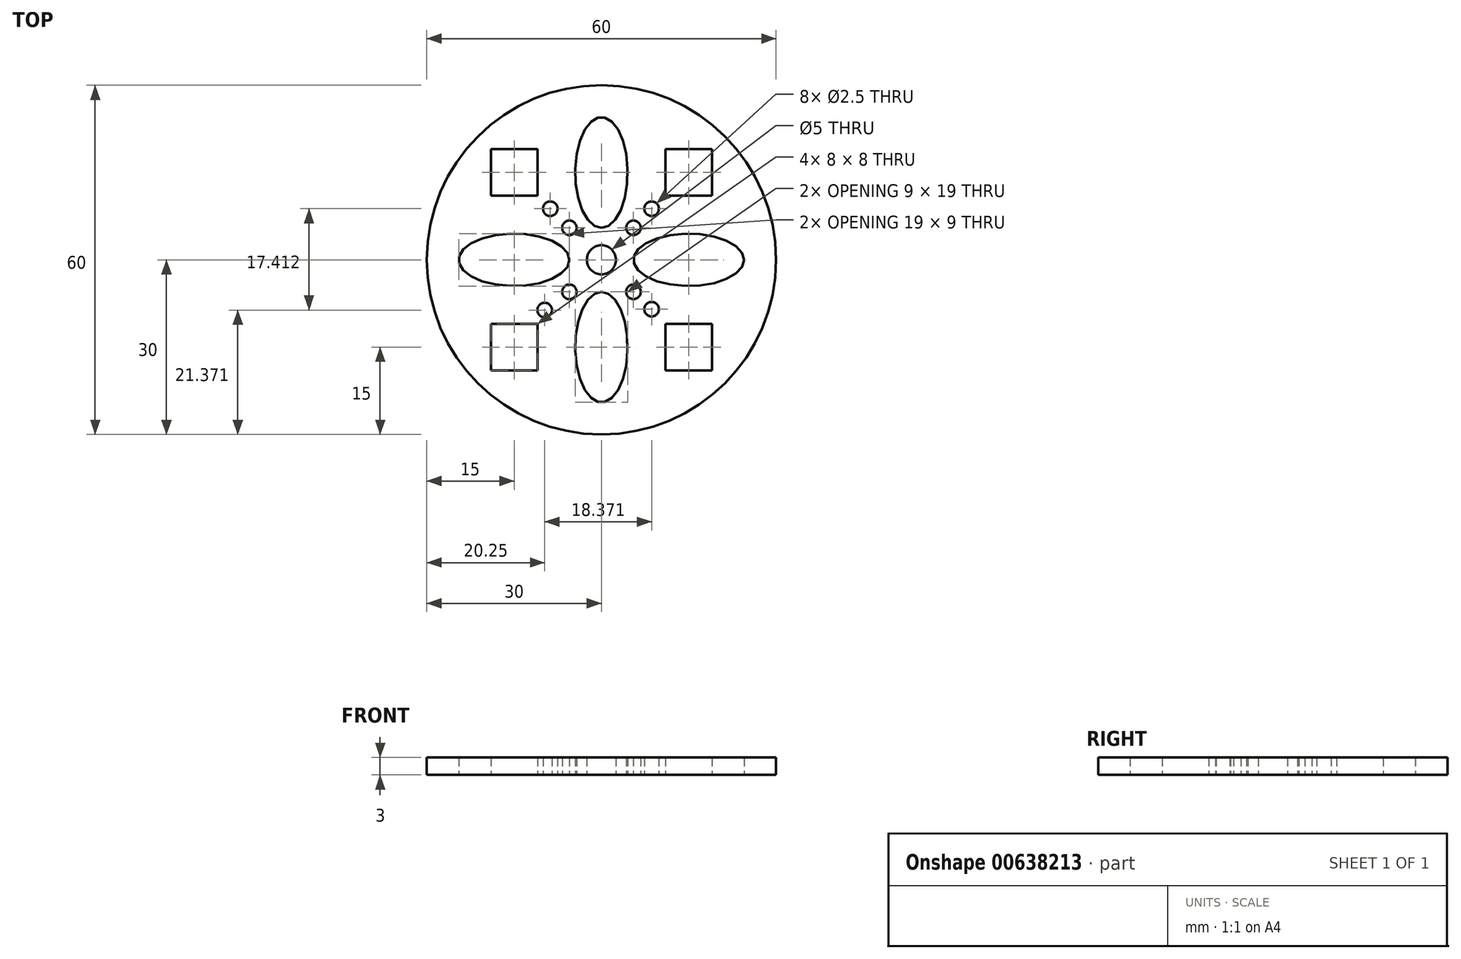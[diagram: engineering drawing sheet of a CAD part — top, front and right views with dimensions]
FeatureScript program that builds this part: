
annotation { "Feature Type Name" : "Feature", "Feature Type Description" : "" }
export const myFeature = defineFeature(function(context is Context, id is Id, definition is map)
    precondition{}
    {
        {
            var Q0;
            Q0=qCreatedBy(makeId("Top.planeOp"),FACE);
            var sketch = newSketch(context, id + "F0", { "sketchPlane" : qUnion([Q0])});
            skCircle(sketch, "E0", {"center": v(0, 0) * mm, "radius": 30 * mm});
            skEllipse(sketch, "E1", {"center": v(0, 15) * mm, "majorRadius": 9.5 * mm, "minorRadius": 4.5 * mm, "majorAxis": v(0, -1)});
            skEllipse(sketch, "E2", {"center": v(15, 0) * mm, "majorRadius": 9.5 * mm, "minorRadius": 4.5 * mm, "majorAxis": v(1, 0)});
            skEllipse(sketch, "E3", {"center": v(-15, 0) * mm, "majorRadius": 9.5 * mm, "minorRadius": 4.5 * mm, "majorAxis": v(1, 0)});
            skPoint(sketch, "E4.endSnap0", {"position": v(-4.5, 15) * mm});
            skPoint(sketch, "E5.positionSnap0", {"position": v(-15, 4.5) * mm});
            skCircle(sketch, "E6", {"center": v(0, 0) * mm, "radius": 2.5 * mm});
            skPoint(sketch, "E7.positionSnap0", {"position": v(15, 4.5) * mm});
            skPoint(sketch, "E8.positionSnap0", {"position": v(4.5, 15) * mm});
            skPoint(sketch, "E9.positionSnap0", {"position": v(-15, -4.5) * mm});
            skPoint(sketch, "E10.positionSnap0", {"position": v(15, -4.5) * mm});
            skLineSegment(sketch, "E11.bottom", {"start": v(-11, 11) * mm, "end": v(-19, 11) * mm});
            skLineSegment(sketch, "E11.top", {"start": v(-11, 19) * mm, "end": v(-19, 19) * mm});
            skLineSegment(sketch, "E11.left", {"start": v(-11, 11) * mm, "end": v(-11, 19) * mm});
            skLineSegment(sketch, "E11.right", {"start": v(-19, 11) * mm, "end": v(-19, 19) * mm});
            skLineSegment(sketch, "E12.bottom", {"start": v(11, 11) * mm, "end": v(19, 11) * mm});
            skLineSegment(sketch, "E12.top", {"start": v(11, 19) * mm, "end": v(19, 19) * mm});
            skLineSegment(sketch, "E12.left", {"start": v(11, 11) * mm, "end": v(11, 19) * mm});
            skLineSegment(sketch, "E12.right", {"start": v(19, 11) * mm, "end": v(19, 19) * mm});
            skPoint(sketch, "E13.positionSnap0", {"position": v(5.5, 0) * mm});
            skPoint(sketch, "E14.positionSnap0", {"position": v(0, 5.5) * mm});
            skPoint(sketch, "E15", {"position": v(5.5, 5.5) * mm});
            skCircle(sketch, "E16", {"center": v(5.5, 5.5) * mm, "radius": 1.25 * mm});
            skPoint(sketch, "E17.positionSnap0", {"position": v(0, -3.99) * mm});
            skEllipse(sketch, "E18", {"center": v(0, -15) * mm, "majorRadius": 9.5 * mm, "minorRadius": 4.5 * mm, "majorAxis": v(0, 1)});
            skPoint(sketch, "E19", {"position": v(5.5, -5.5) * mm});
            skPoint(sketch, "E19.positionSnap0", {"position": v(0, -5.5) * mm});
            skPoint(sketch, "E20", {"position": v(-5.5, -5.5) * mm});
            skPoint(sketch, "E20.positionSnap0", {"position": v(-5.5, 0) * mm});
            skPoint(sketch, "E21", {"position": v(-5.5, 5.5) * mm});
            skCircle(sketch, "E22", {"center": v(-5.5, 5.5) * mm, "radius": 1.25 * mm});
            skCircle(sketch, "E23", {"center": v(-5.5, -5.5) * mm, "radius": 1.25 * mm});
            skCircle(sketch, "E24", {"center": v(5.5, -5.5) * mm, "radius": 1.25 * mm});
            skPoint(sketch, "E25.startSnap0", {"position": v(-4.5, -15) * mm});
            skPoint(sketch, "E26", {"position": v(15, -15) * mm});
            skPoint(sketch, "E26.positionSnap0", {"position": v(4.5, -15) * mm});
            skPoint(sketch, "E27", {"position": v(-15, -15) * mm});
            skLineSegment(sketch, "E28.bottom", {"start": v(19, -11) * mm, "end": v(11, -11) * mm});
            skLineSegment(sketch, "E28.top", {"start": v(19, -19) * mm, "end": v(11, -19) * mm});
            skLineSegment(sketch, "E28.left", {"start": v(19, -11) * mm, "end": v(19, -19) * mm});
            skLineSegment(sketch, "E28.right", {"start": v(11, -11) * mm, "end": v(11, -19) * mm});
            skLineSegment(sketch, "E29.bottom", {"start": v(-11, -19) * mm, "end": v(-19, -19) * mm});
            skLineSegment(sketch, "E29.top", {"start": v(-11, -11) * mm, "end": v(-19, -11) * mm});
            skLineSegment(sketch, "E29.left", {"start": v(-11, -19) * mm, "end": v(-11, -11) * mm});
            skLineSegment(sketch, "E29.right", {"start": v(-19, -19) * mm, "end": v(-19, -11) * mm});
            skCircle(sketch, "E30", {"center": v(8.62, 8.78) * mm, "radius": 1.25 * mm});
            skCircle(sketch, "E31", {"center": v(-8.8, 8.78) * mm, "radius": 1.25 * mm});
            skCircle(sketch, "E32", {"center": v(-9.75, -8.63) * mm, "radius": 1.25 * mm});
            skCircle(sketch, "E33", {"center": v(8.62, -8.48) * mm, "radius": 1.25 * mm});
            skSolve(sketch);
        }
        {
            var Q0;
            Q0=makeQuery(id+"F0.imprint","IMPRINT",FACE,{"disambiguationData":[TD([[makeQuery(id+"F0.imprint","IMPRINT",EDGE,{"derivedFrom":sQuery(id+"F0.wireOp",EDGE,"E0")}),1.0]])]});
            extrude(context, id + "F1", {"entities" : qUnion([Q0]), "depth" : 3 * mm, "offsetDistance" : 25 * mm});
        }
    });
